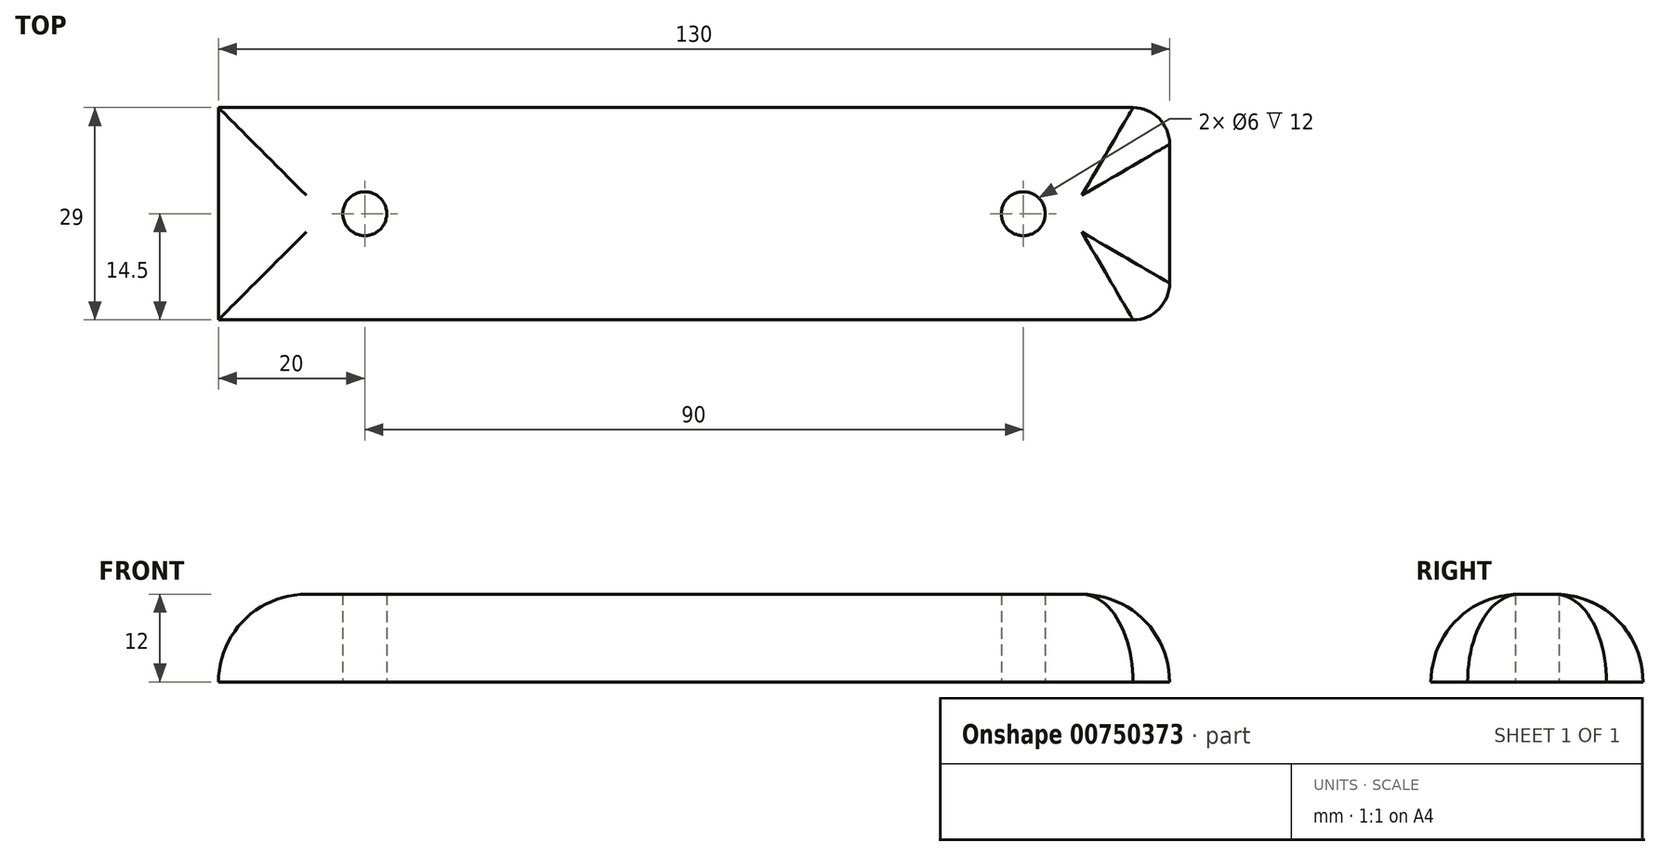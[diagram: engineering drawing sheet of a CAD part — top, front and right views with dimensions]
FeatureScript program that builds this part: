
annotation { "Feature Type Name" : "Feature", "Feature Type Description" : "" }
export const myFeature = defineFeature(function(context is Context, id is Id, definition is map)
    precondition{}
    {
        {
            var Q0;
            Q0=qCreatedBy(makeId("Top.planeOp"),FACE);
            var sketch = newSketch(context, id + "F0", { "sketchPlane" : qUnion([Q0])});
            skLineSegment(sketch, "E0.bottom", {"start": v(-5, 0) * mm, "end": v(-130, 0) * mm});
            skLineSegment(sketch, "E0.top", {"start": v(-5, 29) * mm, "end": v(-130, 29) * mm});
            skLineSegment(sketch, "E0.left", {"start": v(0, 5) * mm, "end": v(0, 24) * mm});
            skLineSegment(sketch, "E0.right", {"start": v(-130, 0) * mm, "end": v(-130, 29) * mm});
            skCircle(sketch, "E1", {"center": v(-110, 14.5) * mm, "radius": 3 * mm});
            skCircle(sketch, "E2", {"center": v(-20, 14.5) * mm, "radius": 3 * mm});
            skPoint(sketch, "E3.orphan", {"position": v(-130, 14.5) * mm});
            skPoint(sketch, "E4.orphan", {"position": v(0, 14.5) * mm});
            skPoint(sketch, "E5.visualSharp", {"position": v(0, 0) * mm});
            skArc(sketch, "E5.filletArc", {"start": v(-5, 0) * mm, "mid": v(-1.46, 1.46) * mm, "end": v(0, 5) * mm});
            skPoint(sketch, "E6.visualSharp", {"position": v(0, 29) * mm});
            skArc(sketch, "E6.filletArc", {"start": v(0, 24) * mm, "mid": v(-1.46, 27.54) * mm, "end": v(-5, 29) * mm});
            skSolve(sketch);
        }
        {
            var Q0;
            Q0=makeQuery(id+"F0.imprint","IMPRINT",FACE,{"disambiguationData":[TD([[makeQuery(id+"F0.imprint","IMPRINT",EDGE,{"derivedFrom":sQuery(id+"F0.wireOp",EDGE,"E0.bottom")}),-1.0]])]});
            extrude(context, id + "F1", {"entities" : qUnion([Q0]), "depth" : 12 * mm, "offsetDistance" : 25 * mm});
        }
        {
            var Q0;
            Q0=makeQuery(id+"F1.opExtrude","CAP_EDGE",EDGE,{"disambiguationData":[OSD([sQuery(id+"F0.wireOp",EDGE,"E0.top")])],"isStart":false});
            var Q1;
            Q1=makeQuery(id+"F1.opExtrude","CAP_EDGE",EDGE,{"disambiguationData":[OSD([sQuery(id+"F0.wireOp",EDGE,"E0.bottom")])],"isStart":false});
            var Q2;
            Q2=makeQuery(id+"F1.opExtrude","CAP_EDGE",EDGE,{"disambiguationData":[OSD([sQuery(id+"F0.wireOp",EDGE,"E0.right")])],"isStart":false});
            var Q3;
            Q3=makeQuery(id+"F1.opExtrude","CAP_EDGE",EDGE,{"disambiguationData":[OSD([sQuery(id+"F0.wireOp",EDGE,"E0.left")])],"isStart":false});
            fillet(context, id + "F2", {"entities" : qUnion([Q0, Q1, Q2, Q3]), "radius" : 12 * mm, "tangentPropagation" : true, "allowEdgeOverflow" : false});
        }
    });
